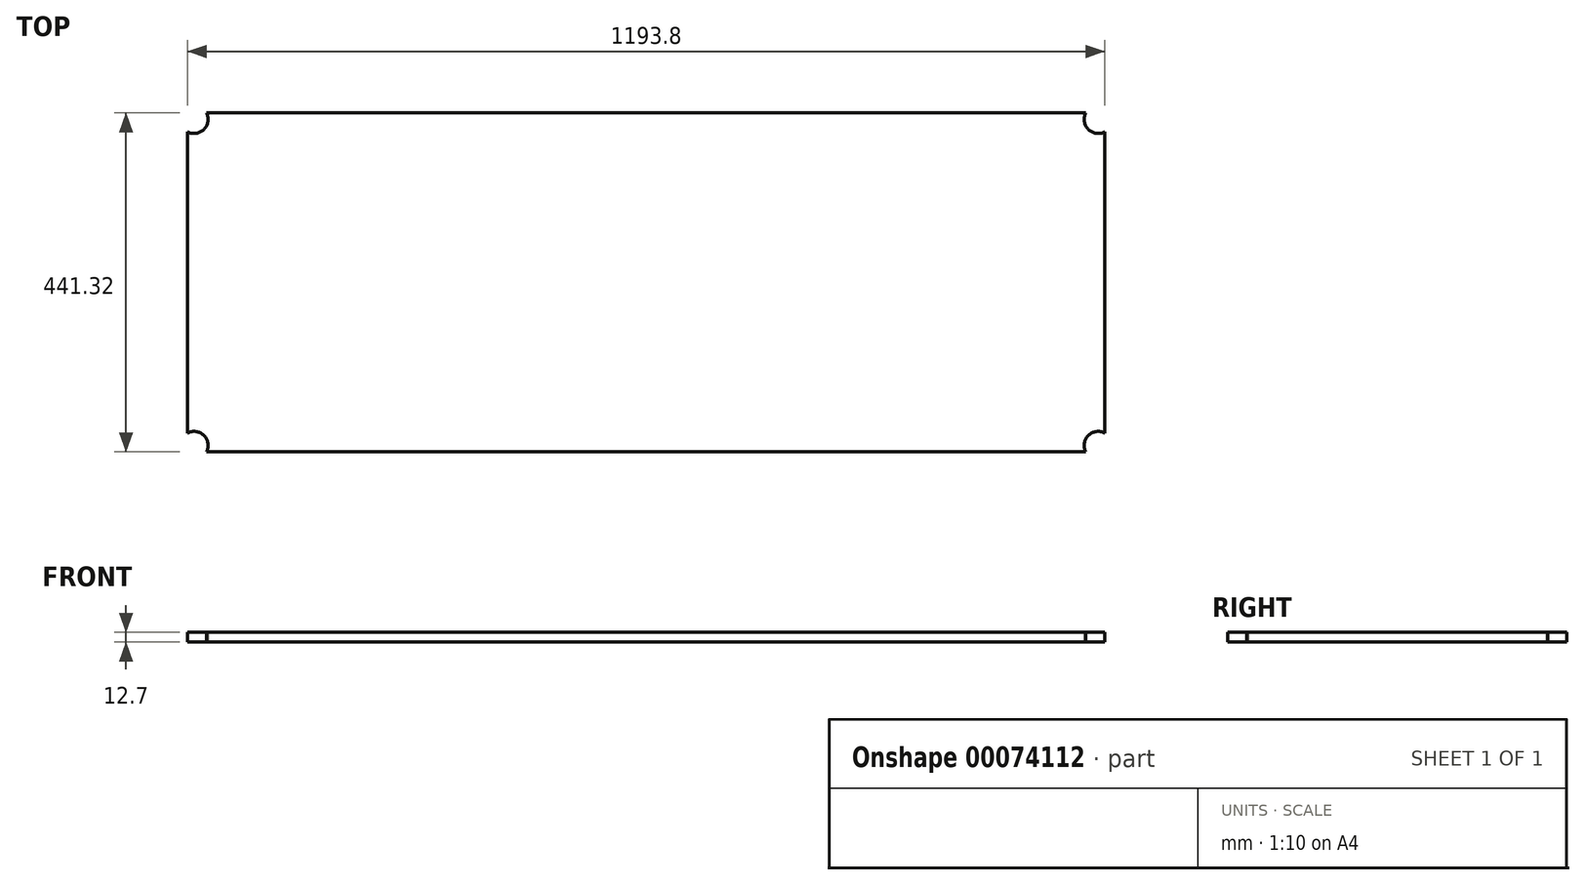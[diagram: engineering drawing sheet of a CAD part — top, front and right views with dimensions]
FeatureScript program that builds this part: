
annotation { "Feature Type Name" : "Feature", "Feature Type Description" : "" }
export const myFeature = defineFeature(function(context is Context, id is Id, definition is map)
    precondition{}
    {
        {
            var Q0;
            Q0=qCreatedBy(makeId("Top.planeOp"),FACE);
            var sketch = newSketch(context, id + "F0", { "sketchPlane" : qUnion([Q0])});
            skLineSegment(sketch, "E0", {"start": v(0, 304.8) * mm, "end": v(0, -304.8) * mm, "construction": true});
            skLineSegment(sketch, "E1", {"start": v(762, 0) * mm, "end": v(-762, 0) * mm, "construction": true});
            skSolve(sketch);
        }
        {
            var Q0;
            Q0=qCreatedBy(makeId("Top.planeOp"),FACE);
            var sketch = newSketch(context, id + "F1", { "sketchPlane" : qUnion([Q0])});
            skCircle(sketch, "E2", {"center": v(588.45, 212.22) * mm, "radius": 16.7 * mm, "construction": true});
            skCircle(sketch, "E3", {"center": v(588.45, 212.22) * mm, "radius": 17.97 * mm, "construction": true});
            skCircle(sketch, "E4.MirrorC", {"center": v(588.45, -212.22) * mm, "radius": 16.7 * mm, "construction": true});
            skCircle(sketch, "E5.MirrorC", {"center": v(588.45, -212.22) * mm, "radius": 17.97 * mm, "construction": true});
            skCircle(sketch, "E6.MirrorC", {"center": v(-588.45, 212.22) * mm, "radius": 17.97 * mm, "construction": true});
            skCircle(sketch, "E7.MirrorC", {"center": v(-588.45, 212.22) * mm, "radius": 16.7 * mm, "construction": true});
            skCircle(sketch, "E8.MirrorC", {"center": v(-588.45, -212.22) * mm, "radius": 17.97 * mm, "construction": true});
            skCircle(sketch, "E9.MirrorC", {"center": v(-588.45, -212.22) * mm, "radius": 16.7 * mm, "construction": true});
            skSolve(sketch);
        }
        {
            var Q0;
            Q0=qCreatedBy(makeId("Top.planeOp"),FACE);
            var sketch = newSketch(context, id + "F2", { "sketchPlane" : qUnion([Q0])});
            skLineSegment(sketch, "E10.bottom", {"start": v(604.84, -228.6) * mm, "end": v(-604.84, -228.6) * mm, "construction": true});
            skLineSegment(sketch, "E10.top", {"start": v(604.84, 228.6) * mm, "end": v(-604.84, 228.6) * mm, "construction": true});
            skLineSegment(sketch, "E10.left", {"start": v(604.84, -228.6) * mm, "end": v(604.84, 228.6) * mm, "construction": true});
            skLineSegment(sketch, "E10.right", {"start": v(-604.84, -228.6) * mm, "end": v(-604.84, 228.6) * mm, "construction": true});
            skPoint(sketch, "E10.middle", {"position": v(0, 0) * mm});
            skLineSegment(sketch, "E11.0", {"start": v(598.49, -222.25) * mm, "end": v(-598.49, -222.25) * mm, "construction": true});
            skLineSegment(sketch, "E11.1", {"start": v(598.49, -222.25) * mm, "end": v(598.49, 222.25) * mm, "construction": true});
            skLineSegment(sketch, "E11.2", {"start": v(598.49, 222.25) * mm, "end": v(-598.49, 222.25) * mm, "construction": true});
            skLineSegment(sketch, "E11.3", {"start": v(-598.49, -222.25) * mm, "end": v(-598.49, 222.25) * mm, "construction": true});
            skSolve(sketch);
        }
        {
            var Q0;
            Q0=qCreatedBy(makeId("Top.planeOp"),FACE);
            var sketch = newSketch(context, id + "F3", { "sketchPlane" : qUnion([Q0])});
            skLineSegment(sketch, "E12.0", {"start": v(596.9, -220.66) * mm, "end": v(-596.9, -220.66) * mm, "construction": true});
            skLineSegment(sketch, "E12.1", {"start": v(596.9, -220.66) * mm, "end": v(596.9, 220.66) * mm, "construction": true});
            skLineSegment(sketch, "E12.2", {"start": v(596.9, 220.66) * mm, "end": v(-596.9, 220.66) * mm, "construction": true});
            skLineSegment(sketch, "E12.3", {"start": v(-596.9, -220.66) * mm, "end": v(-596.9, 220.66) * mm, "construction": true});
            skCircle(sketch, "E13.0", {"center": v(588.45, 212.22) * mm, "radius": 18.29 * mm, "construction": true});
            skCircle(sketch, "E14.0", {"center": v(588.45, -212.22) * mm, "radius": 18.29 * mm, "construction": true});
            skCircle(sketch, "E15.0", {"center": v(-588.45, 212.22) * mm, "radius": 18.29 * mm, "construction": true});
            skCircle(sketch, "E16.0", {"center": v(-588.45, -212.22) * mm, "radius": 18.29 * mm, "construction": true});
            skSolve(sketch);
        }
        {
            var Q0;
            Q0=qCreatedBy(makeId("Top.planeOp"),FACE);
            var sketch = newSketch(context, id + "F4", { "sketchPlane" : qUnion([Q0])});
            skLineSegment(sketch, "E17", {"start": v(-572.23, 220.66) * mm, "end": v(572.23, 220.66) * mm});
            skLineSegment(sketch, "E18", {"start": v(-596.9, 196) * mm, "end": v(-596.9, -196) * mm});
            skLineSegment(sketch, "E19.MirrorCS", {"start": v(-572.23, -220.66) * mm, "end": v(572.23, -220.66) * mm});
            skLineSegment(sketch, "E20.MirrorCS", {"start": v(-596.9, -196) * mm, "end": v(-596.9, 196) * mm});
            skLineSegment(sketch, "E21.MirrorCS", {"start": v(596.9, -196) * mm, "end": v(596.9, 196) * mm});
            skArc(sketch, "E22", {"start": v(572.23, 220.66) * mm, "mid": v(575.52, 199.29) * mm, "end": v(596.9, 196) * mm});
            skArc(sketch, "E23.MirrorCS", {"start": v(572.23, -220.66) * mm, "mid": v(575.52, -199.29) * mm, "end": v(596.9, -196) * mm});
            skArc(sketch, "E24.MirrorCS", {"start": v(-572.23, 220.66) * mm, "mid": v(-575.52, 199.29) * mm, "end": v(-596.9, 196) * mm});
            skArc(sketch, "E25.MirrorCS", {"start": v(-572.23, -220.66) * mm, "mid": v(-575.52, -199.29) * mm, "end": v(-596.9, -196) * mm});
            skSolve(sketch);
        }
        {
            var Q0;
            Q0=makeQuery(id+"F4.imprint","IMPRINT",FACE,{"disambiguationData":[TD([[makeQuery(id+"F4.imprint","IMPRINT",EDGE,{"derivedFrom":sQuery(id+"F4.wireOp",EDGE,"E17")}),-1.0]])]});
            extrude(context, id + "F5", {"entities" : qUnion([Q0]), "depth" : 12.7 * mm});
        }
        {
            var Q0;
            Q0=qCreatedBy(makeId("Top.planeOp"),FACE);
            var sketch = newSketch(context, id + "F6", { "sketchPlane" : qUnion([Q0])});
            skLineSegment(sketch, "E26", {"start": v(554.15, 220.66) * mm, "end": v(596.9, 177.9) * mm});
            skLineSegment(sketch, "E27.MirrorCS", {"start": v(554.15, -220.66) * mm, "end": v(596.9, -177.9) * mm});
            skLineSegment(sketch, "E28.MirrorCS", {"start": v(-554.15, -220.66) * mm, "end": v(-596.9, -177.9) * mm});
            skLineSegment(sketch, "E29.MirrorCS", {"start": v(-554.15, 220.66) * mm, "end": v(-596.9, 177.9) * mm});
            skLineSegment(sketch, "E30", {"start": v(596.9, 177.9) * mm, "end": v(596.9, -177.9) * mm});
            skLineSegment(sketch, "E31", {"start": v(554.15, 220.66) * mm, "end": v(-554.15, 220.66) * mm});
            skLineSegment(sketch, "E32.MirrorCS", {"start": v(554.15, -220.66) * mm, "end": v(-554.15, -220.66) * mm});
            skLineSegment(sketch, "E33.MirrorCS", {"start": v(-596.9, 177.9) * mm, "end": v(-596.9, -177.9) * mm});
            skSolve(sketch);
        }
        {
            var Q0;
            Q0=makeQuery(id+"F6.imprint","IMPRINT",FACE,{"disambiguationData":[TD([[makeQuery(id+"F6.imprint","IMPRINT",EDGE,{"derivedFrom":sQuery(id+"F6.wireOp",EDGE,"E26")}),-1.0]])]});
            extrude(context, id + "F7", {"entities" : qUnion([Q0]), "depth" : 1 / 203.2 * mm});
        }
    });
